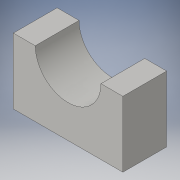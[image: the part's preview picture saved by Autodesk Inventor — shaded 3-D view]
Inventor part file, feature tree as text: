
AUTODESK INVENTOR PART (.ipt)
format: ipt  version: 2016 (Build 200138000, 138)  size: 98,304 bytes
history: native  units: in
note: dims shown in document units (in); Inventor stores cm internally (conversion verified against a paired STEP export)
features: extrude x2, sketch x2
ambient origin geometry x8: Origin, YZ Plane, XZ Plane, XY Plane, X Axis, Y Axis, Z Axis, Center Point
bodies: Solid1 (feature_tree)
feature tree (4):
  extrude  "Extrusion1"  Depth=1.5in
  extrude  "Extrusion2"  Depth=1.5in
  sketch  "Sketch1"  dims[d0=2.5in d1=1.5in]
  sketch  "Sketch2"  dims[d2=1.0in d3=0.0in d4=1.5in d5=1.0in d6=0.0in]
